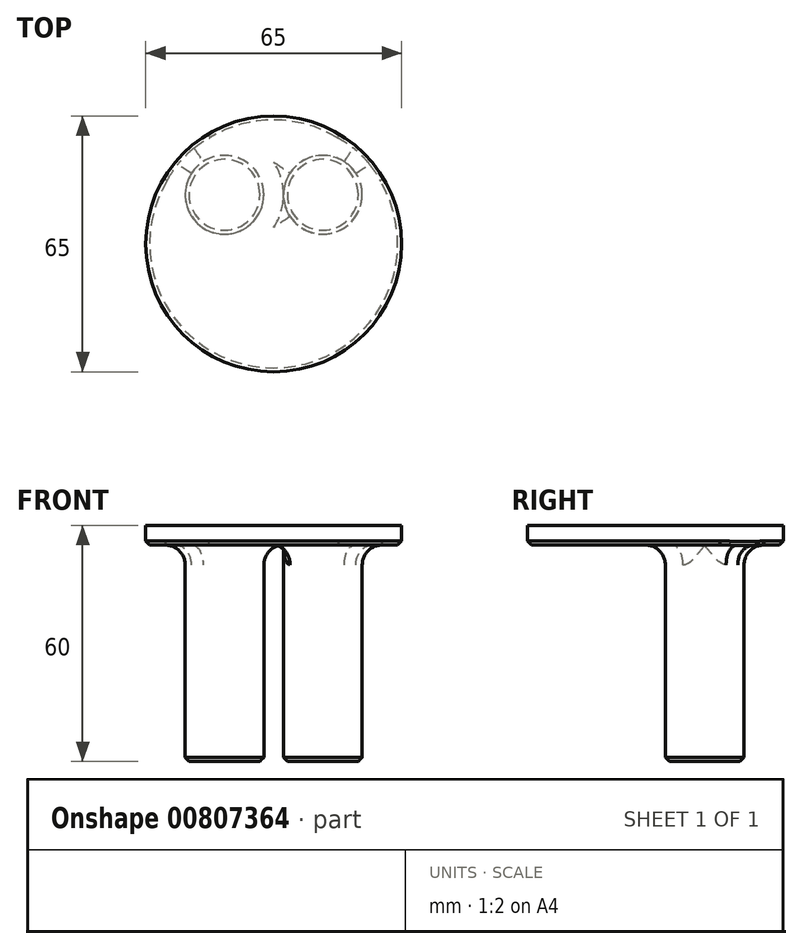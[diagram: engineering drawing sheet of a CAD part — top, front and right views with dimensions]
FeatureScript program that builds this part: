
annotation { "Feature Type Name" : "Feature", "Feature Type Description" : "" }
export const myFeature = defineFeature(function(context is Context, id is Id, definition is map)
    precondition{}
    {
        {
            var Q0;
            Q0=qCreatedBy(makeId("Top.planeOp"),FACE);
            var sketch = newSketch(context, id + "F0", { "sketchPlane" : qUnion([Q0])});
            skCircle(sketch, "E0", {"center": v(0, 0) * mm, "radius": 32.5 * mm});
            skSolve(sketch);
        }
        {
            var Q0;
            Q0 = qSketchRegion(id + "F0", true);
            extrude(context, id + "F1", {"entities" : qUnion([Q0]), "oppositeDirection" : true, "depth" : 5 * mm, "offsetDistance" : 25 * mm});
        }
        {
            var Q0;
            Q0=qCreatedBy(makeId("Top.planeOp"),FACE);
            var sketch = newSketch(context, id + "F2", { "sketchPlane" : qUnion([Q0])});
            skCircle(sketch, "E1", {"center": v(-12.5, 12.5) * mm, "radius": 10 * mm});
            skSolve(sketch);
        }
        {
            var Q0;
            Q0=qCreatedBy(makeId("Top.planeOp"),FACE);
            var sketch = newSketch(context, id + "F3", { "sketchPlane" : qUnion([Q0])});
            skCircle(sketch, "E2", {"center": v(12.5, 12.5) * mm, "radius": 10 * mm});
            skSolve(sketch);
        }
        {
            var Q0;
            Q0=makeQuery(id+"F2.imprint","IMPRINT",FACE,{"disambiguationData":[TD([[makeQuery(id+"F2.imprint","IMPRINT",EDGE,{"derivedFrom":sQuery(id+"F2.wireOp",EDGE,"E1")}),1.0]])]});
            extrude(context, id + "F4", {"entities" : qUnion([Q0]), "operationType" : NewBodyOperationType.ADD, "oppositeDirection" : true, "depth" : 60 * mm, "offsetDistance" : 25 * mm});
        }
        {
            var Q0;
            Q0 = qSketchRegion(id + "F3", true);
            extrude(context, id + "F5", {"entities" : qUnion([Q0]), "operationType" : NewBodyOperationType.ADD, "oppositeDirection" : true, "depth" : 60 * mm, "offsetDistance" : 25 * mm});
        }
        {
            var Q0;
            Q0=makeQuery(id+"F4.boolean.opBoolean","INTERSECT",EDGE,{"derivedFrom":[makeQuery(id+"F1.opExtrude","CAP_FACE",FACE,{"disambiguationData":[OSD([sQuery(id+"F0.wireOp",EDGE,"E0")])],"isStart":false}),makeQuery(id+"F4.opExtrude","SWEPT_FACE",FACE,{"disambiguationData":[OSD([sQuery(id+"F2.wireOp",EDGE,"E1")])]})]});
            fillet(context, id + "F6", {"entities" : qUnion([Q0]), "radius" : 5 * mm, "tangentPropagation" : true, "allowEdgeOverflow" : false});
        }
        {
            var Q0;
            Q0=makeQuery(id+"F5.boolean.opBoolean","INTERSECT",EDGE,{"derivedFrom":[makeQuery(id+"F1.opExtrude","CAP_FACE",FACE,{"disambiguationData":[OSD([sQuery(id+"F0.wireOp",EDGE,"E0")])],"isStart":false}),makeQuery(id+"F5.opExtrude","SWEPT_FACE",FACE,{"disambiguationData":[OSD([sQuery(id+"F3.wireOp",EDGE,"E2")])]})]});
            fillet(context, id + "F7", {"entities" : qUnion([Q0]), "radius" : 5 * mm, "tangentPropagation" : true, "allowEdgeOverflow" : false});
        }
        {
            var Q0;
            Q0=makeQuery(id+"F4.opExtrude","CAP_EDGE",EDGE,{"disambiguationData":[OSD([sQuery(id+"F2.wireOp",EDGE,"E1")])],"isStart":false});
            var Q1;
            Q1=makeQuery(id+"F5.opExtrude","CAP_EDGE",EDGE,{"disambiguationData":[OSD([sQuery(id+"F3.wireOp",EDGE,"E2")])],"isStart":false});
            chamfer(context, id + "F8", {"entities" : qUnion([Q0, Q1]), "width" : 1 * mm, "tangentPropagation" : true});
        }
        {
            var Q0;
            Q0=makeQuery(id+"F1.opExtrude","CAP_EDGE",EDGE,{"disambiguationData":[OSD([sQuery(id+"F0.wireOp",EDGE,"E0")])],"isStart":false});
            chamfer(context, id + "F9", {"entities" : qUnion([Q0]), "width" : 1 * mm, "tangentPropagation" : true});
        }
    });
